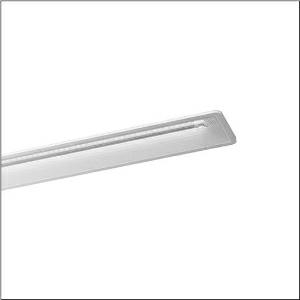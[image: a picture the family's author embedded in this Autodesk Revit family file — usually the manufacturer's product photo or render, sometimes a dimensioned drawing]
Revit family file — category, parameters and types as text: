
# Revit family: taris_r__21_5mt115d04wd_a05d
name_source: partatom
category: Lighting Fixtures
units: mm (PartAtom-declared; Revit-internal decimal feet)

## family parameters
Cut with Voids When Loaded = No
Host = Face
Light Source = No
Part Type = Normal
Room Calculation Point = No
Round Connector Dimension = Use Diameter
Shared = No

## types (1)
- --- (1 x LED, 3680 lm, 22.2 W, 4000K)
    Apparent Load = 22 VA
    CIE Flux Codes = 73 96 99 100 100
    Color Rendering = 80
    Color Temperature = 4000K
    Default Elevation = 1800 mm
    Description = Taris® 21, office luminaire, primary anti-glare with micro louvre, primary optical cover: axial lens, of PMMA, structured, CAT 2 (L<= 1500cd/m²), light emission: direct distribution, primary light characteristic: symmetric, installation type: recessed, LED rated luminous flux: 3.680 lm, light colour: 840, colour temperature: 4000K, control gear: ECG DALI, with terminal, 5-pole, mains connection: 230V, AC, 50Hz, rated input power: 22W, housing, luminaire housing, of plastic, traffic white (RAL 9016), length: 968 mm, width: 150 mm, height: 76mm, recess depth: 106 mm, protection rating (complete): IP20, insulation class (complete): insulation class I (protective earthing), certification: CE, ENEC, VDE, protection symbol: F, impact resistance: IK02, permissible ambient temperature for indoor applications: 0..+35°C, standard: EN 50419, packaging unit: 1 piece
    Height = 0 mm  [stored 0 ft]
    Lamp = 1 x LED
    Lamp Light Flux = 3680 lm
    Lamp Power = 22.2 W
    Lamp count = 1
    Length = 962 mm
    Luminous efficacy = 166 lm/W
    Manufacturer = Siteco
    ModVariant = No
    Model = 5MT115D04WD
    Mounting Place = Ceiling
    Mounting Type = Recessed
    Number of Poles = 1
    OnlyDefault = Yes
    Power Factor = 1
    Product Name = Taris® 21
    Product group = office luminaire | ceiling recessed
    ProductGroupID = 400
    Protection Class = Protection class I
    Protection Degree = IP 20
    RLX_Detail_Level = 1
    RlxData = <blob elided: 29617 chars, md5=55e1b59e>
    Socket = socket
    Standby Power = 0 W
    System Light Flux = 3680 lm
    System Power = 22 W
    Type Comments = factory setting: luminous flux: 100 % | dim-lin: 254 | 200 mA
    Type Image = l_1004723.jpg
    URL = http://relux.com
    VarID = @adj_130235
    Voltage = 0 V
    Weight = 0.00 kg
    Width = 144 mm

note: [stored X ft] marks values corroborated as IEEE doubles in the binary element streams (Revit-internal decimal feet)

## geometry (parser evidence)
native form markers: Blend x4, Sweep x11
no freeform markers — native parametric forms only
